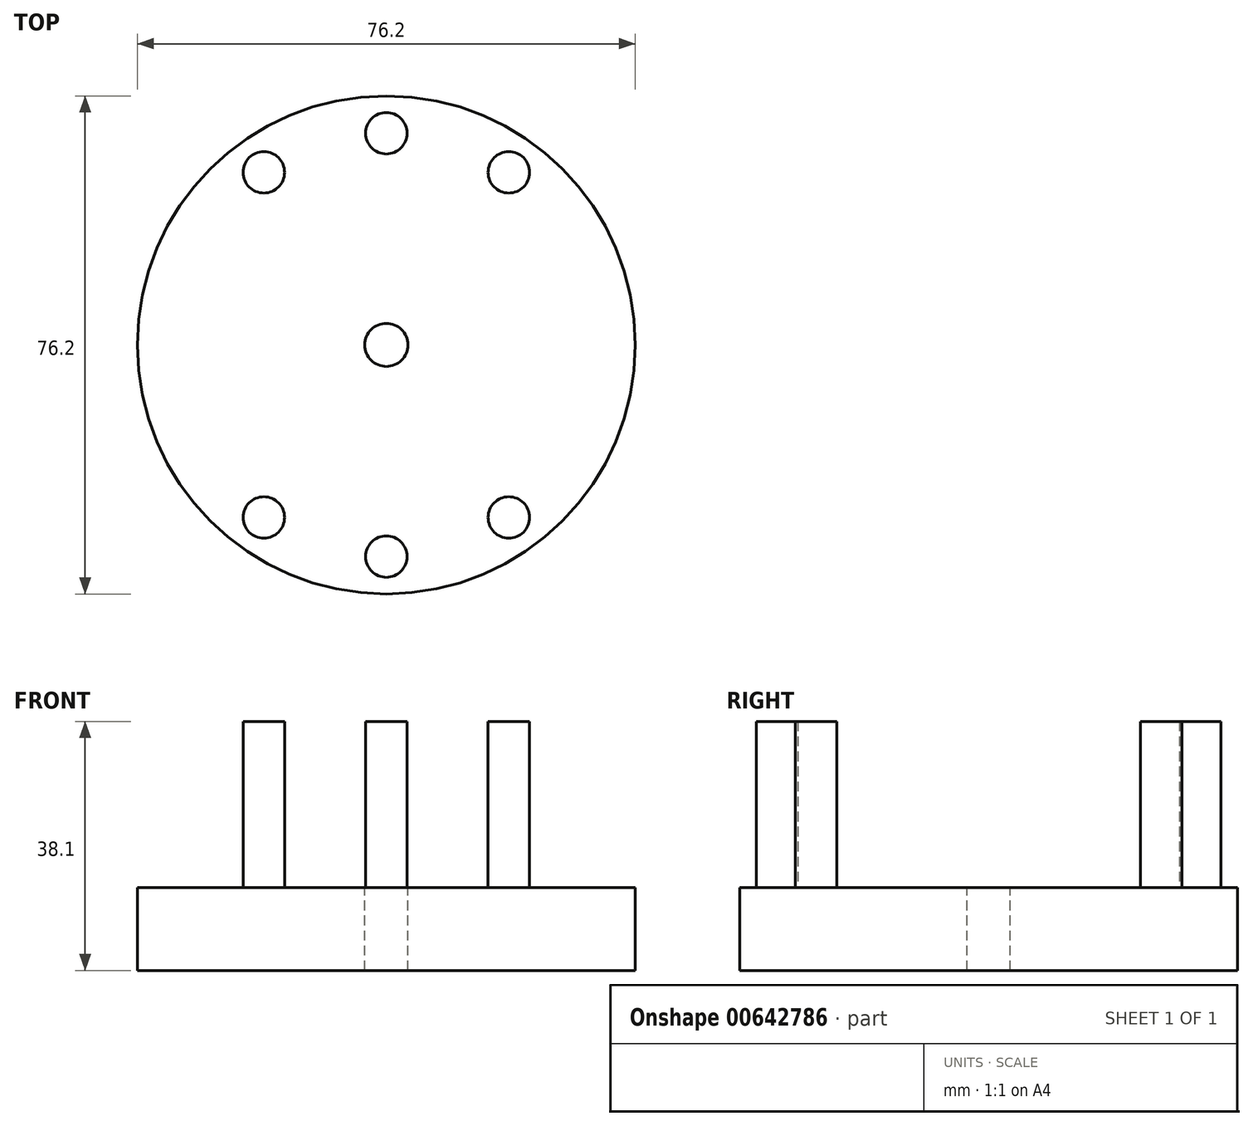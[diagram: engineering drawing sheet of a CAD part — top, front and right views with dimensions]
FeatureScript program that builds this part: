
annotation { "Feature Type Name" : "Feature", "Feature Type Description" : "" }
export const myFeature = defineFeature(function(context is Context, id is Id, definition is map)
    precondition{}
    {
        {
            var Q0;
            Q0=qCreatedBy(makeId("Top.planeOp"),FACE);
            var sketch = newSketch(context, id + "F0", { "sketchPlane" : qUnion([Q0])});
            skCircle(sketch, "E0", {"center": v(0, 0) * mm, "radius": 38.1 * mm});
            skSolve(sketch);
        }
        {
            var Q0;
            Q0 = qSketchRegion(id + "F0", true);
            extrude(context, id + "F1", {"entities" : qUnion([Q0]), "depth" : 12.7 * mm, "offsetDistance" : 25.4 * mm});
        }
        {
            var Q0;
            Q0=makeQuery(id+"F1.opExtrude","CAP_FACE",FACE,{"disambiguationData":[OSD([sQuery(id+"F0.wireOp",EDGE,"E0")])],"isStart":false});
            var sketch = newSketch(context, id + "F2", { "sketchPlane" : qUnion([Q0])});
            skCircle(sketch, "E1", {"center": v(0, 32.39) * mm, "radius": 3.18 * mm});
            skCircle(sketch, "E2", {"center": v(-18.75, 26.4) * mm, "radius": 3.18 * mm});
            skCircle(sketch, "E3", {"center": v(18.75, 26.4) * mm, "radius": 3.18 * mm});
            skSolve(sketch);
        }
        {
            var Q0;
            Q0 = qSketchRegion(id + "F2", true);
            extrude(context, id + "F3", {"entities" : qUnion([Q0]), "operationType" : NewBodyOperationType.ADD, "depth" : 25.4 * mm, "offsetDistance" : 25.4 * mm});
        }
        {
            var Q0;
            Q0=makeQuery(id+"F1.opExtrude","CAP_FACE",FACE,{"disambiguationData":[OSD([sQuery(id+"F0.wireOp",EDGE,"E0")])],"isStart":false});
            var sketch = newSketch(context, id + "F4", { "sketchPlane" : qUnion([Q0])});
            skCircle(sketch, "E4", {"center": v(-18.75, -26.4) * mm, "radius": 3.18 * mm});
            skCircle(sketch, "E5", {"center": v(0, -32.39) * mm, "radius": 3.18 * mm});
            skCircle(sketch, "E6", {"center": v(18.75, -26.4) * mm, "radius": 3.18 * mm});
            skSolve(sketch);
        }
        {
            var Q0;
            Q0 = qSketchRegion(id + "F4", true);
            extrude(context, id + "F5", {"entities" : qUnion([Q0]), "operationType" : NewBodyOperationType.ADD, "depth" : 25.4 * mm, "offsetDistance" : 25.4 * mm});
        }
        {
            var Q0;
            Q0=makeQuery(id+"F1.opExtrude","CAP_FACE",FACE,{"disambiguationData":[OSD([sQuery(id+"F0.wireOp",EDGE,"E0")])],"isStart":false});
            var sketch = newSketch(context, id + "F6", { "sketchPlane" : qUnion([Q0])});
            skCircle(sketch, "E7", {"center": v(0, 0) * mm, "radius": 3.3 * mm});
            skSolve(sketch);
        }
        {
            var Q0;
            Q0 = qSketchRegion(id + "F6", true);
            extrude(context, id + "F7", {"entities" : qUnion([Q0]), "operationType" : NewBodyOperationType.REMOVE, "oppositeDirection" : true, "depth" : 12.7 * mm, "offsetDistance" : 25.4 * mm});
        }
    });
